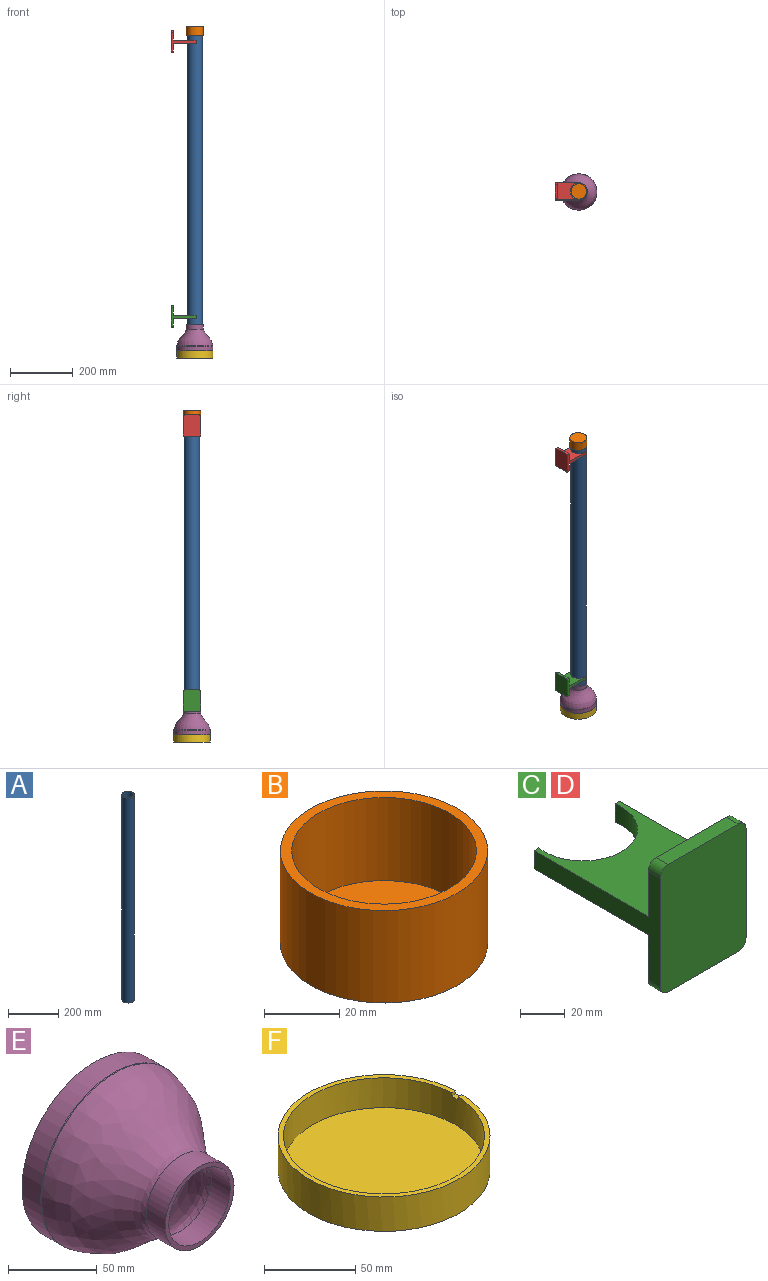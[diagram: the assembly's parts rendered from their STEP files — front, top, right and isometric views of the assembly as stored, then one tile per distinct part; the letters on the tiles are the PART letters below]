
ASSEMBLY  parts=6 mates=5
PART A: 46 faces, bbox 49x49x1000 mm
  f0: cylinder r=21.5mm len=1000mm, axis (0,0,-1), area 134956.6mm2, adj f2,f3,f4,f5,f6,f7,f8,f9
  f1: cylinder r=24.5mm len=1000mm, axis (0,0,-1), area 153806.1mm2, adj f2,f3,f4,f5,f6,f7,f8,f9
  f2: plane 49x49mm, normal (0,0,1), area 433.5mm2, adj f0,f1
  f3: plane 49x49mm, normal (0,0,-1), area 433.5mm2, adj f0,f1
  f4: cylinder r=1mm len=3.02mm, axis (-1,0,0), area 18.9mm2, adj f0,f1
  f5: cylinder r=1mm len=3.02mm, axis (-1,0,0), area 18.9mm2, adj f0,f1
  f6: cylinder r=1mm len=3.02mm, axis (-1,0,0), area 18.9mm2, adj f0,f1
  f7: cylinder r=1mm len=3.02mm, axis (-1,0,0), area 18.9mm2, adj f0,f1
  f8: cylinder r=1mm len=3.02mm, axis (-1,0,0), area 18.9mm2, adj f0,f1
  f9: cylinder r=1mm len=3.02mm, axis (-1,0,0), area 18.9mm2, adj f0,f1
  f10: cylinder r=1mm len=3.02mm, axis (-1,0,0), area 18.9mm2, adj f0,f1
  f11: cylinder r=1mm len=3.02mm, axis (-1,0,0), area 18.9mm2, adj f0,f1
  f12: cylinder r=1mm len=3.02mm, axis (-1,0,0), area 18.9mm2, adj f0,f1
  f13: cylinder r=1mm len=3.02mm, axis (-1,0,0), area 18.9mm2, adj f0,f1
  f14: cylinder r=1mm len=3.02mm, axis (-1,0,0), area 18.9mm2, adj f0,f1
  f15: cylinder r=1mm len=3.02mm, axis (-1,0,0), area 18.9mm2, adj f0,f1
  f16: cylinder r=1mm len=3.02mm, axis (-1,0,0), area 18.9mm2, adj f0,f1
  f17: cylinder r=1mm len=3.02mm, axis (-1,0,0), area 18.9mm2, adj f0,f1
  f18: cylinder r=1mm len=3.02mm, axis (-1,0,0), area 18.9mm2, adj f0,f1
  f19: cylinder r=1mm len=3.02mm, axis (-1,0,0), area 18.9mm2, adj f0,f1
  f20: cylinder r=1mm len=3.02mm, axis (-1,0,0), area 18.9mm2, adj f0,f1
  f21: cylinder r=1mm len=3.02mm, axis (-1,0,0), area 18.9mm2, adj f0,f1
  f22: cylinder r=1mm len=3.02mm, axis (-1,0,0), area 18.9mm2, adj f0,f1
  f23: cylinder r=1mm len=3.02mm, axis (-1,0,0), area 18.9mm2, adj f0,f1
  f24: cylinder r=1mm len=3.02mm, axis (-1,0,0), area 18.9mm2, adj f0,f1
  f25: cylinder r=1mm len=3.02mm, axis (-1,0,0), area 18.9mm2, adj f0,f1
  f26: cylinder r=1mm len=3.02mm, axis (-1,0,0), area 18.9mm2, adj f0,f1
  f27: cylinder r=1mm len=3.02mm, axis (-1,0,0), area 18.9mm2, adj f0,f1
  f28: cylinder r=1mm len=3.02mm, axis (-1,0,0), area 18.9mm2, adj f0,f1
  f29: cylinder r=1mm len=3.02mm, axis (-1,0,0), area 18.9mm2, adj f0,f1
  f30: cylinder r=1mm len=3.02mm, axis (-1,0,0), area 18.9mm2, adj f0,f1
  f31: cylinder r=1mm len=3.02mm, axis (-1,0,0), area 18.9mm2, adj f0,f1
  f32: cylinder r=1mm len=3.02mm, axis (-1,0,0), area 18.9mm2, adj f0,f1
  f33: cylinder r=1mm len=3.02mm, axis (-1,0,0), area 18.9mm2, adj f0,f1
  f34: cylinder r=1mm len=3.02mm, axis (-1,0,0), area 18.9mm2, adj f0,f1
  f35: cylinder r=1mm len=3.02mm, axis (-1,0,0), area 18.9mm2, adj f0,f1
  f36: cylinder r=1mm len=3.02mm, axis (-1,0,0), area 18.9mm2, adj f0,f1
  f37: cylinder r=1mm len=3.02mm, axis (-1,0,0), area 18.9mm2, adj f0,f1
  f38: cylinder r=1mm len=3.02mm, axis (-1,0,0), area 18.9mm2, adj f0,f1
  f39: cylinder r=1mm len=3.02mm, axis (-1,0,0), area 18.9mm2, adj f0,f1
  f40: cylinder r=1mm len=3.02mm, axis (-1,0,0), area 18.9mm2, adj f0,f1
  f41: cylinder r=1mm len=3.02mm, axis (-1,0,0), area 18.9mm2, adj f0,f1
  f42: cylinder r=1mm len=3.02mm, axis (-1,0,0), area 18.9mm2, adj f0,f1
  f43: cylinder r=1mm len=3.02mm, axis (-1,0,0), area 18.9mm2, adj f0,f1
  f44: cylinder r=1mm len=3.02mm, axis (-1,0,0), area 18.9mm2, adj f0,f1
  f45: cylinder r=1mm len=3.02mm, axis (-1,0,0), area 18.9mm2, adj f0,f1
PART B: 5 faces, bbox 55x55x30 mm
  f0: plane 49x49mm, normal (0,0,1), area 1885.7mm2, adj f1
  f1: cylinder r=24.5mm len=49mm, axis (0,0,-1), area 4156.3mm2, adj f0,f3
  f2: cylinder r=27.5mm len=55mm, axis (0,0,-1), area 5183.6mm2, adj f3,f4
  f3: plane 55x55mm, normal (0,0,1), area 490.1mm2, adj f1,f2
  f4: plane 55x55mm, normal (0,0,-1), area 2375.8mm2, adj f2
PART C: 16 faces, bbox 54.5x80x70 mm
  f0: plane 72.48x54.46mm, normal (0,0,-1), area 2817.5mm2, adj f1,f2,f4,f5,f6,f10
  f1: plane 10x3.03mm, normal (0,1,0), area 30.3mm2, adj f0,f2,f6,f7
  f2: plane 80x60mm, normal (-1,0,0), area 1176.2mm2, adj f0,f1,f3,f7,f8,f10,f12,f14
  f3: plane 70x54.46mm, normal (0,-1,0), area 3791mm2, adj f2,f4,f9,f11,f12,f13,f14,f15
  f4: plane 80x60mm, normal (1,0,0), area 1176.2mm2, adj f0,f3,f5,f7,f8,f10,f13,f15
  f5: plane 10x3.03mm, normal (0,1,0), area 30.3mm2, adj f0,f4,f6,f7
  f6: cylinder r=24.5mm len=49mm, axis (0,0,-1), area 846.6mm2, adj f0,f1,f5,f7
  f7: plane 72.48x54.46mm, normal (0,0,1), area 2817.5mm2, adj f1,f2,f4,f5,f6,f8
  f8: plane 54.46x30mm, normal (0,1,0), area 1623.2mm2, adj f2,f4,f7,f9,f14,f15
  f9: plane 44.46x7.52mm, normal (0,0,1), area 334.6mm2, adj f3,f8,f14,f15
  f10: plane 54.46x30mm, normal (0,1,0), area 1623.2mm2, adj f0,f2,f4,f11,f12,f13
  f11: plane 44.46x7.52mm, normal (0,0,-1), area 334.6mm2, adj f3,f10,f12,f13
  f12: cylinder r=5mm len=7.52mm, axis (0,-1,0), area 59.1mm2, adj f2,f3,f10,f11
  f13: cylinder r=5mm len=7.52mm, axis (0,1,0), area 59.1mm2, adj f3,f4,f10,f11
  f14: cylinder r=5mm len=7.52mm, axis (0,1,0), area 59.1mm2, adj f2,f3,f8,f9
  f15: cylinder r=5mm len=7.52mm, axis (0,-1,0), area 59.1mm2, adj f3,f4,f8,f9
PART D: same geometry as C
PART E: 9 faces, bbox 116x83.6x116 mm
  f0: cylinder r=27.5mm len=55mm, axis (0,-1,0), area 2590.1mm2, adj f1,f8
  f1: revolved ~115.88x115.88mm, area 17112.4mm2, adj f0,f2
  f2: cone r=57.94mm half-angle=5.8deg, axis (0,1,0), area 219.5mm2, adj f1,f3
  f3: cylinder r=58mm len=116mm, axis (0,-1,0), area 5466.4mm2, adj f2,f4
  f4: plane 116x116mm, normal (0,1,0), area 1065mm2, adj f3,f5
  f5: cylinder r=55mm len=110mm, axis (0,-1,0), area 5183.6mm2, adj f4,f6
  f6: revolved ~110x110mm, area 15984.2mm2, adj f5,f7
  f7: cylinder r=24.5mm len=49mm, axis (0,-1,0), area 2309.1mm2, adj f6,f8
  f8: plane 55x55mm, normal (0,-1,0), area 490.1mm2, adj f0,f7
PART F: 8 faces, bbox 116x116x23 mm
  f0: cylinder r=55mm len=110mm, axis (0,0,-1), area 6901.5mm2, adj f2,f4,f5,f6,f7
  f1: cylinder r=58mm len=116mm, axis (0,0,-1), area 8371.8mm2, adj f2,f3,f5,f6,f7
  f2: plane 116x115.95mm, normal (0,0,1), area 1050mm2, adj f0,f1,f6,f7
  f3: plane 116x116mm, normal (0,0,-1), area 10568.3mm2, adj f1
  f4: plane 110x110mm, normal (0,0,1), area 9503.3mm2, adj f0
  f5: plane 5.01x3.06mm, normal (0,0,1), area 15mm2, adj f0,f1,f6,f7
  f6: plane 3x2mm, normal (0,-1,0), area 6mm2, adj f0,f1,f2,f5
  f7: plane 3x2mm, normal (0,1,0), area 6mm2, adj f0,f1,f2,f5
PLACE A t=(-77.5,562.22,833.76)mm
PLACE B rot(axis=(1,0,0),180deg) t=(-77.5,562.22,1838.76)mm
PLACE C rot(axis=(0,0,-1),90deg) t=(-77.5,562.22,903.76)mm
PLACE D rot(axis=(0,0,-1),90deg) t=(-77.5,562.22,1783.76)mm
PLACE E rot(axis=(-1,0,0),90deg) t=(-77.5,562.22,883.76)mm
PLACE F t=(-77.5,562.22,777.13)mm
MATE fastened D.f6 <-> A.f1  axis (0,0,-1) through (-77.5,562.22,1783.76)mm
MATE fastened E.f0 <-> A.f0  axis (0,0,1) through (-77.5,562.22,883.76)mm
MATE fastened B.f1 <-> A.f0  axis (0,0,-1) through (-77.5,562.22,1808.76)mm
MATE fastened F.f1 <-> E.f0  axis (0,0,1) through (-77.5,562.22,800.13)mm
MATE fastened C.f6 <-> B.f2  axis (0,0,-1) through (-77.5,562.22,903.76)mm
